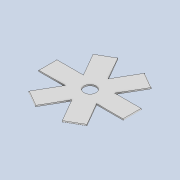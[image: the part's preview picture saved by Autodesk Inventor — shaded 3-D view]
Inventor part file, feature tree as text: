
AUTODESK INVENTOR PART (.ipt)
format: ipt  version: 2020 (Build 240168000, 168)  size: 112,128 bytes
history: native  units: mm
features: extrude x3, sketch x3, pattern_circular x1
ambient origin geometry x8: Origin, YZ Plane, XZ Plane, XY Plane, X Axis, Y Axis, Z Axis, Center Point
bodies: Solid1 (feature_tree)
feature tree (7):
  extrude  "Extrusion1"  Depth=0.2mm TaperAngle=0.0deg
  extrude  "Extrusion2"  Depth=0.1mm
  pattern_circular  "Circular Pattern1"  [2 undecoded]
  extrude  "Extrusion3"  Depth=3.0mm TaperAngle=360.0deg
  sketch  "Sketch1"  dims[d0=3.0mm d1=0.2mm d2=0.0mm]
  sketch  "Sketch2"  dims[d3=0.1mm d4=7.0mm]
  sketch  "Sketch3"  dims[d5=0.2mm d6=3.0mm d7=0.0mm d8=60.0mm d9=360.0deg d11=2.0mm d12=3.0mm d13=0.0mm]
note: 2 required parameter values undecoded (feature->parameter linkage not recoverable at this tier; creation-order binding heuristic only, values carry confidence <= 0.55)
